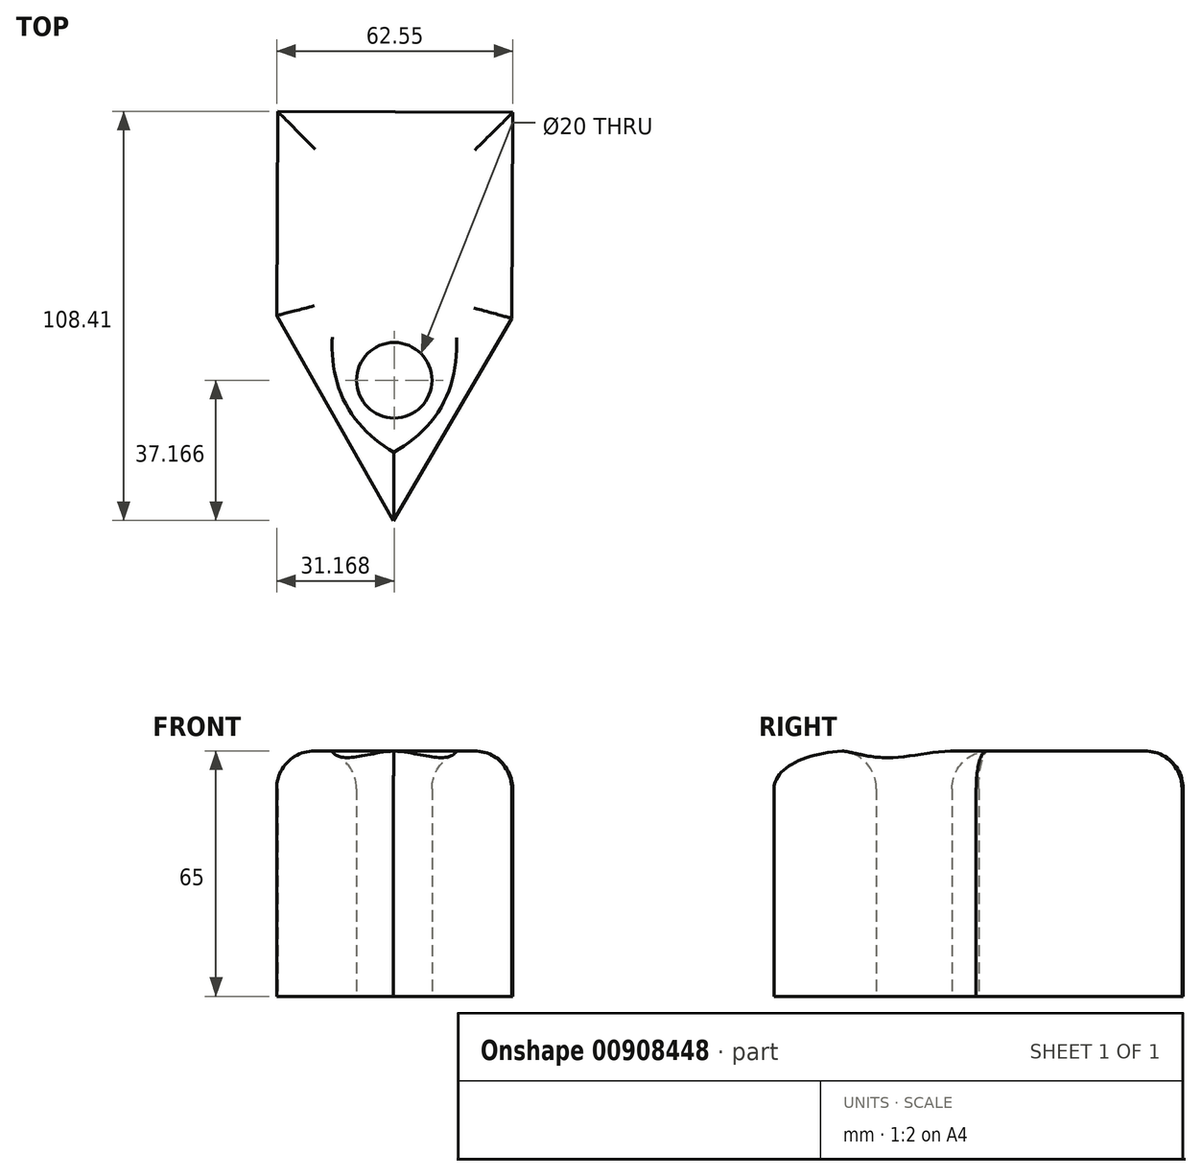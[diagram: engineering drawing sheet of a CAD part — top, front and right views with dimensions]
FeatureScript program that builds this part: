
annotation { "Feature Type Name" : "Feature", "Feature Type Description" : "" }
export const myFeature = defineFeature(function(context is Context, id is Id, definition is map)
    precondition{}
    {
        {
            var Q0;
            Q0=qCreatedBy(makeId("Top.planeOp"),FACE);
            var sketch = newSketch(context, id + "F0", { "sketchPlane" : qUnion([Q0])});
            skCircle(sketch, "E0.cCircle", {"center": v(0, 0) * mm, "radius": 36.08 * mm, "construction": true});
            skPoint(sketch, "E0.0.midPoint", {"position": v(18.43, -31.02) * mm});
            skLineSegment(sketch, "E1", {"start": v(-36.86, 62.05) * mm, "end": v(0, 0) * mm});
            skCircle(sketch, "E2", {"center": v(-17.88, 30.1) * mm, "radius": 10 * mm});
            skLineSegment(sketch, "E3", {"start": v(0, 0) * mm, "end": v(18.43, -31.02) * mm});
            skCircle(sketch, "E4", {"center": v(9.21, -15.51) * mm, "radius": 10 * mm});
            skLineSegment(sketch, "E5", {"start": v(-36.09, 0) * mm, "end": v(-8.25, -46.87) * mm});
            skLineSegment(sketch, "E6", {"start": v(17.65, 31.47) * mm, "end": v(45.3, -15.06) * mm});
            skLineSegment(sketch, "E7", {"start": v(-36.86, 62.05) * mm, "end": v(-36.09, 0) * mm});
            skLineSegment(sketch, "E8", {"start": v(-36.86, 62.05) * mm, "end": v(17.65, 31.47) * mm});
            skLineSegment(sketch, "E9", {"start": v(-8.25, -46.87) * mm, "end": v(45.3, -15.06) * mm});
            skSolve(sketch);
        }
        {
            var Q0;
            Q0=qSketchRegion(id+"F0",true);
            extrude(context, id + "F1", {"entities" : qUnion([Q0]), "depth" : 50 * mm, "offsetDistance" : 25 * mm});
        }
        {
            var Q0;
            {var subQ0=sQuery(id+"F0.wireOp",EDGE,"E2");var subQ1=sQuery(id+"F0.wireOp",EDGE,"E1");var subQ2=makeQuery(id+"F0.imprint","INTERSECT",VERTEX,{"disambiguationData":[OD(0.0)],"derivedFrom":[subQ1,subQ0]});Q0=makeQuery(id+"F0.imprint","IMPRINT",FACE,{"disambiguationData":[TD([[makeQuery(id+"F0.imprint","IMPRINT",EDGE,{"disambiguationData":[TD([[subQ2,-1.0]])],"derivedFrom":subQ1}),1.0]])]});}
            var Q1;
            {var subQ0=sQuery(id+"F0.wireOp",EDGE,"E2");var subQ1=sQuery(id+"F0.wireOp",EDGE,"E1");var subQ2=makeQuery(id+"F0.imprint","INTERSECT",VERTEX,{"disambiguationData":[OD(0.0)],"derivedFrom":[subQ1,subQ0]});Q1=makeQuery(id+"F0.imprint","IMPRINT",FACE,{"disambiguationData":[TD([[makeQuery(id+"F0.imprint","IMPRINT",EDGE,{"disambiguationData":[TD([[subQ2,-1.0]])],"derivedFrom":subQ1}),-1.0]])]});}
            var Q2;
            {var subQ0=sQuery(id+"F0.wireOp",EDGE,"E4");var subQ1=sQuery(id+"F0.wireOp",EDGE,"E3");var subQ2=makeQuery(id+"F0.imprint","INTERSECT",VERTEX,{"disambiguationData":[OD(0.0)],"derivedFrom":[subQ1,subQ0]});Q2=makeQuery(id+"F0.imprint","IMPRINT",FACE,{"disambiguationData":[TD([[makeQuery(id+"F0.imprint","IMPRINT",EDGE,{"disambiguationData":[TD([[subQ2,-1.0]])],"derivedFrom":subQ1}),-1.0]])]});}
            var Q3;
            {var subQ0=sQuery(id+"F0.wireOp",EDGE,"E4");var subQ1=sQuery(id+"F0.wireOp",EDGE,"E3");var subQ2=makeQuery(id+"F0.imprint","INTERSECT",VERTEX,{"disambiguationData":[OD(0.0)],"derivedFrom":[subQ1,subQ0]});Q3=makeQuery(id+"F0.imprint","IMPRINT",FACE,{"disambiguationData":[TD([[makeQuery(id+"F0.imprint","IMPRINT",EDGE,{"disambiguationData":[TD([[subQ2,-1.0]])],"derivedFrom":subQ1}),1.0]])]});}
            extrude(context, id + "F2", {"entities" : qUnion([Q0, Q1, Q2, Q3]), "operationType" : NewBodyOperationType.ADD, "depth" : 65 * mm, "offsetDistance" : 25 * mm});
        }
        {
            var Q0;
            Q0=makeQuery(id+"F2.opExtrude","CAP_FACE",FACE,{"disambiguationData":[OSD([sQuery(id+"F0.wireOp",EDGE,"E2")])],"isStart":false});
            var Q1;
            Q1=makeQuery(id+"F2.opExtrude","CAP_EDGE",EDGE,{"disambiguationData":[OSD([sQuery(id+"F0.wireOp",EDGE,"E4")])],"isStart":false});
            fillet(context, id + "F3", {"entities" : qUnion([Q0, Q1]), "radius" : 10 * mm, "tangentPropagation" : true, "allowEdgeOverflow" : false});
        }
        {
            var Q0;
            Q0=makeQuery(id+"F1.opExtrude","SWEPT_BODY",BODY,{"disambiguationData":[OSD([sQuery(id+"F0.wireOp",EDGE,"E2"),sQuery(id+"F0.wireOp",EDGE,"E4"),sQuery(id+"F0.wireOp",EDGE,"E5"),sQuery(id+"F0.wireOp",EDGE,"E6"),sQuery(id+"F0.wireOp",EDGE,"E7"),sQuery(id+"F0.wireOp",EDGE,"E8"),sQuery(id+"F0.wireOp",EDGE,"E9")])]});
            transform(context, id + "F4", {"entities" : qUnion([Q0]), "transformType" : TransformType.TRANSLATION_3D, "dx" : -45.5 * mm, "dy" : 15 * mm, "dz" : 0 * mm, "makeCopy" : false});
        }
        {
            var Q0;
            Q0=makeQuery(id+"F1.opExtrude","SWEPT_BODY",BODY,{"disambiguationData":[OSD([sQuery(id+"F0.wireOp",EDGE,"E2"),sQuery(id+"F0.wireOp",EDGE,"E4"),sQuery(id+"F0.wireOp",EDGE,"E5"),sQuery(id+"F0.wireOp",EDGE,"E6"),sQuery(id+"F0.wireOp",EDGE,"E7"),sQuery(id+"F0.wireOp",EDGE,"E8"),sQuery(id+"F0.wireOp",EDGE,"E9")])]});
            var Q1;
            Q1=makeQuery(id+"F1.opExtrude","SWEPT_EDGE",EDGE,{"disambiguationData":[OSD([sQuery(id+"F0.wireOp",EDGE,"E6"),sQuery(id+"F0.wireOp",EDGE,"E9")])]});
            transform(context, id + "F5", {"entities" : qUnion([Q0]), "transformType" : TransformType.ROTATION, "transformAxis" : qUnion([Q1]), "angle" : 149 * degree, "oppositeDirection" : true, "makeCopy" : false});
        }
    });
